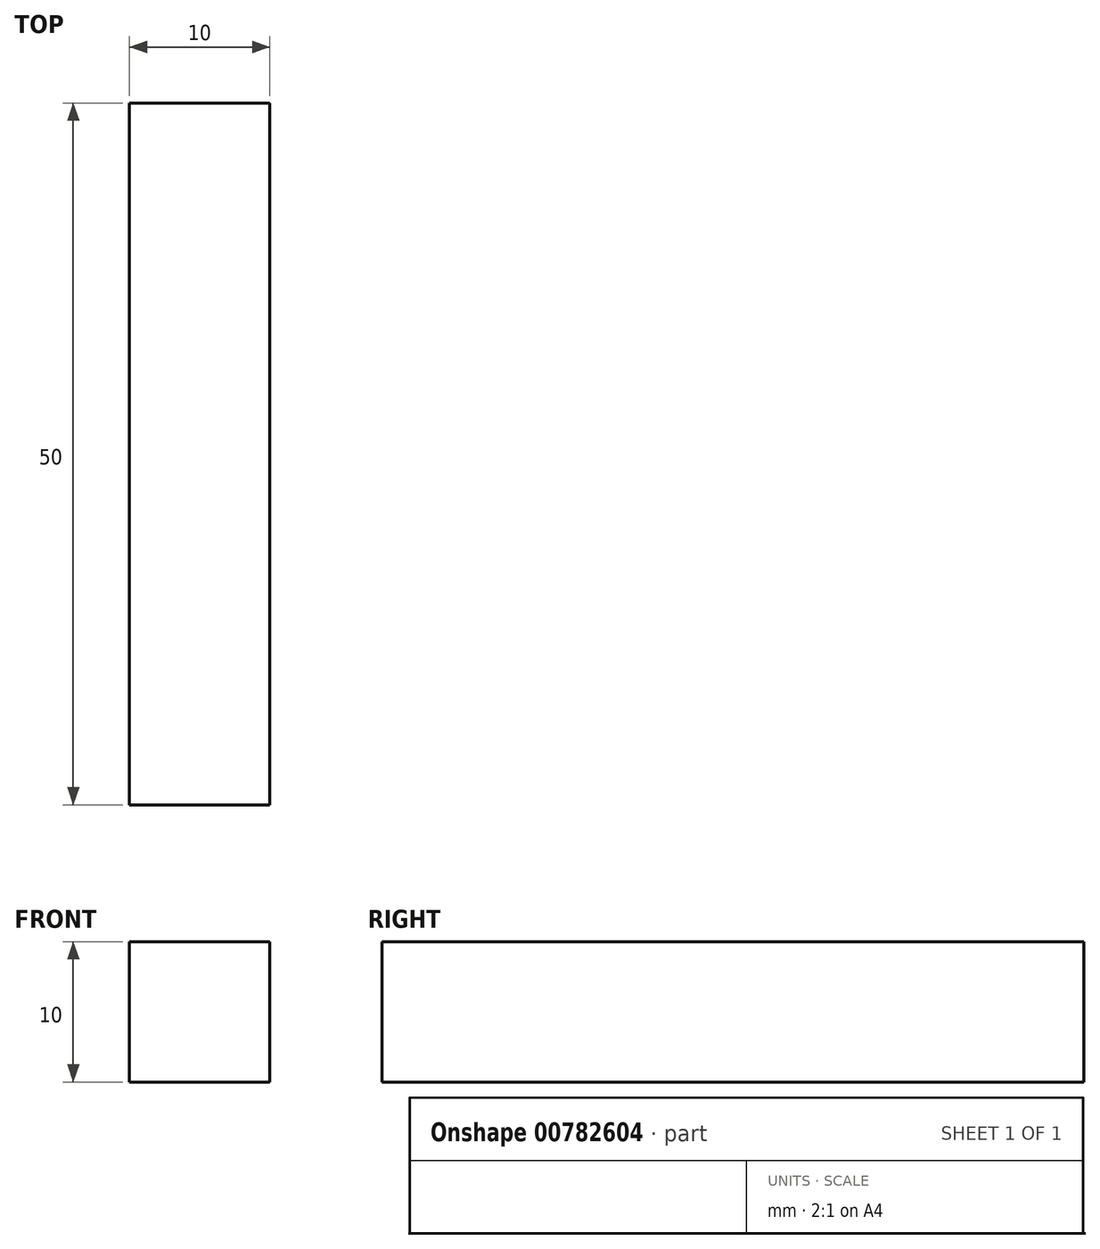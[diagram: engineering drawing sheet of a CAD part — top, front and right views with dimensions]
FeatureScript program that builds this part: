
annotation { "Feature Type Name" : "Feature", "Feature Type Description" : "" }
export const myFeature = defineFeature(function(context is Context, id is Id, definition is map)
    precondition{}
    {
        {
            var Q0;
            Q0=qCreatedBy(makeId("Top.planeOp"),FACE);
            var sketch = newSketch(context, id + "F0", { "sketchPlane" : qUnion([Q0])});
            skLineSegment(sketch, "E0.bottom", {"start": v(-51.42, 23.31) * mm, "end": v(-61.42, 23.31) * mm});
            skLineSegment(sketch, "E0.top", {"start": v(-51.42, 73.31) * mm, "end": v(-61.42, 73.31) * mm});
            skLineSegment(sketch, "E0.left", {"start": v(-51.42, 23.31) * mm, "end": v(-51.42, 73.31) * mm});
            skLineSegment(sketch, "E0.right", {"start": v(-61.42, 23.31) * mm, "end": v(-61.42, 73.31) * mm});
            skPoint(sketch, "E0.middle", {"position": v(-56.42, 48.31) * mm});
            skSolve(sketch);
        }
        {
            var Q0;
            Q0 = qSketchRegion(id + "F0", true);
            extrude(context, id + "F1", {"entities" : qUnion([Q0]), "depth" : 10 * mm, "offsetDistance" : 25 * mm});
        }
    });
